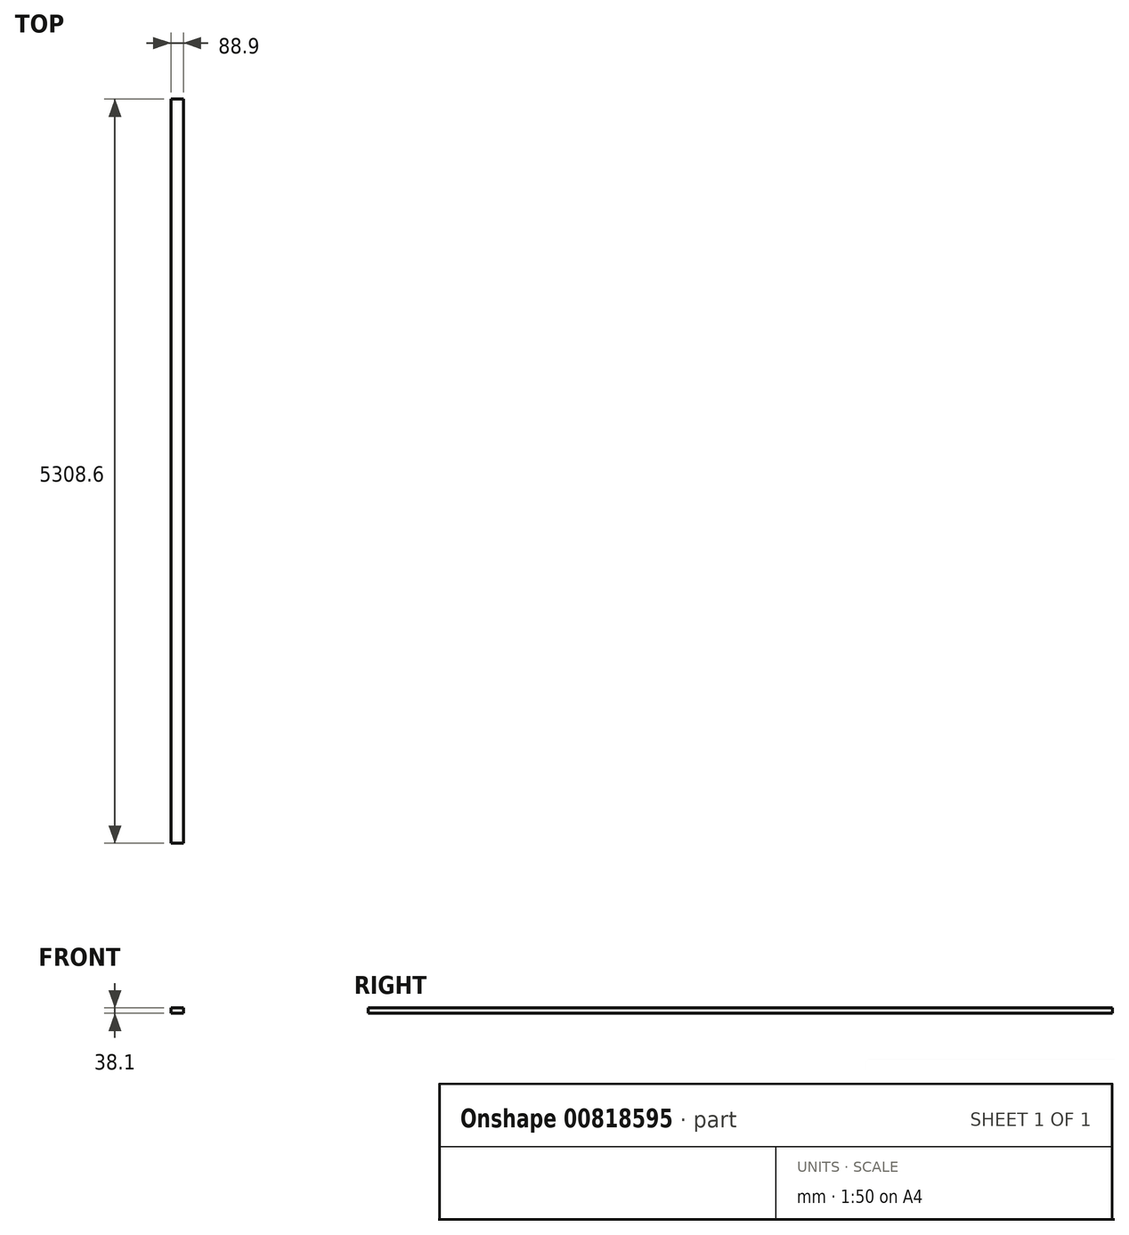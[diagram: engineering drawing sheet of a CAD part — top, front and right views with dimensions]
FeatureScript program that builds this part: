
annotation { "Feature Type Name" : "Feature", "Feature Type Description" : "" }
export const myFeature = defineFeature(function(context is Context, id is Id, definition is map)
    precondition{}
    {
        {
            var Q0;
            Q0=qCreatedBy(makeId("Top.planeOp"),FACE);
            var sketch = newSketch(context, id + "F0", { "sketchPlane" : qUnion([Q0])});
            skLineSegment(sketch, "E0.bottom", {"start": v(-29.27, 0) * mm, "end": v(59.63, 0) * mm});
            skLineSegment(sketch, "E0.top", {"start": v(-29.27, 5308.6) * mm, "end": v(59.63, 5308.6) * mm});
            skLineSegment(sketch, "E0.left", {"start": v(-29.27, 0) * mm, "end": v(-29.27, 5308.6) * mm});
            skLineSegment(sketch, "E0.right", {"start": v(59.63, 0) * mm, "end": v(59.63, 5308.6) * mm});
            skSolve(sketch);
        }
        {
            var Q0;
            Q0 = qSketchRegion(id + "F0", true);
            extrude(context, id + "F1", {"entities" : qUnion([Q0]), "depth" : 38.1 * mm, "offsetDistance" : 25.4 * mm});
        }
    });
